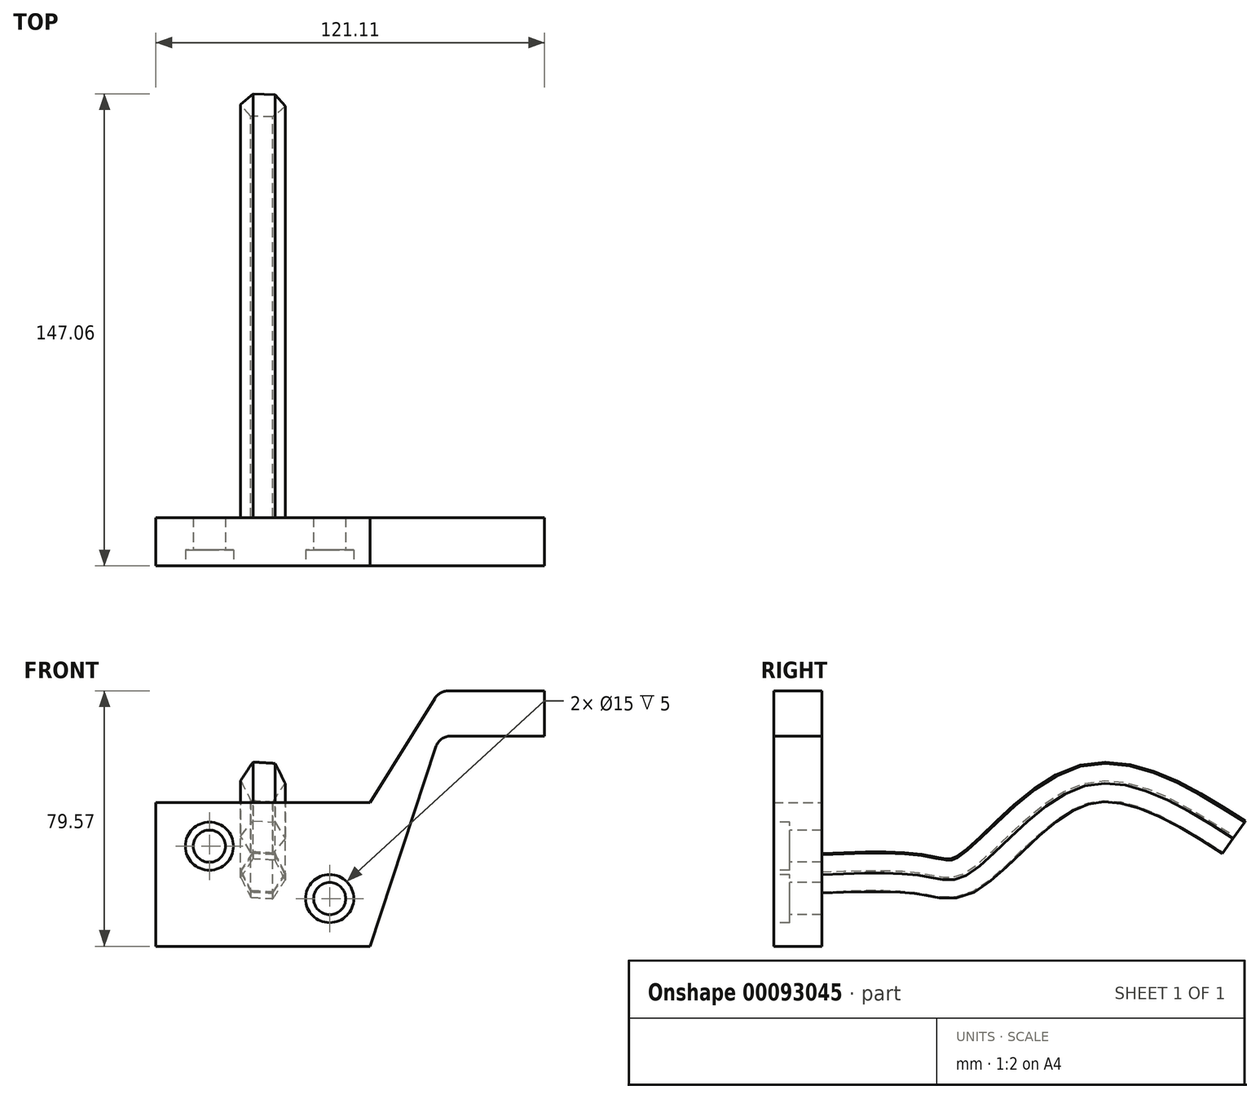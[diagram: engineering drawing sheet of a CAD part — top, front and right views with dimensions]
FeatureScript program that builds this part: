
annotation { "Feature Type Name" : "Feature", "Feature Type Description" : "" }
export const myFeature = defineFeature(function(context is Context, id is Id, definition is map)
    precondition{}
    {
        {
            var Q0;
            Q0=qCreatedBy(makeId("Front.planeOp"),FACE);
            var sketch = newSketch(context, id + "F0", { "sketchPlane" : qUnion([Q0])});
            skLineSegment(sketch, "E0.bottom", {"start": v(33.35, 22.38) * mm, "end": v(-33.35, 22.38) * mm});
            skLineSegment(sketch, "E0.top", {"start": v(33.35, -22.38) * mm, "end": v(-33.35, -22.38) * mm});
            skLineSegment(sketch, "E0.right", {"start": v(-33.35, 22.38) * mm, "end": v(-33.35, -22.38) * mm});
            skPoint(sketch, "E0.middle", {"position": v(0, 0) * mm});
            skLineSegment(sketch, "E1.bottom", {"start": v(87.76, 43.15) * mm, "end": v(55, 43.15) * mm});
            skLineSegment(sketch, "E1.top", {"start": v(87.76, 57.2) * mm, "end": v(55, 57.2) * mm});
            skLineSegment(sketch, "E1.left", {"start": v(87.76, 43.15) * mm, "end": v(87.76, 57.2) * mm});
            skPoint(sketch, "E1.middle", {"position": v(71.38, 50.17) * mm});
            skLineSegment(sketch, "E2", {"start": v(33.35, 22.38) * mm, "end": v(55, 57.2) * mm});
            skLineSegment(sketch, "E3", {"start": v(33.35, -22.38) * mm, "end": v(55, 43.15) * mm});
            skSolve(sketch);
        }
        {
            var Q0;
            Q0=makeQuery(id+"F0.imprint","IMPRINT",FACE,{"disambiguationData":[TD([[makeQuery(id+"F0.imprint","IMPRINT",EDGE,{"derivedFrom":sQuery(id+"F0.wireOp",EDGE,"E0.bottom")}),1.0]])]});
            extrude(context, id + "F1", {"entities" : qUnion([Q0]), "endBound" : BoundingType.SYMMETRIC, "depth" : 15 * mm});
        }
        {
            var Q0;
            Q0=makeQuery(id+"F1.opExtrude","CAP_FACE",FACE,{"disambiguationData":[OSD([sQuery(id+"F0.wireOp",EDGE,"E0.bottom"),sQuery(id+"F0.wireOp",EDGE,"E0.top"),sQuery(id+"F0.wireOp",EDGE,"E0.right"),sQuery(id+"F0.wireOp",EDGE,"E1.bottom"),sQuery(id+"F0.wireOp",EDGE,"E1.top"),sQuery(id+"F0.wireOp",EDGE,"E1.left"),sQuery(id+"F0.wireOp",EDGE,"E2"),sQuery(id+"F0.wireOp",EDGE,"E3")])],"isStart":false});
            var sketch = newSketch(context, id + "F2", { "sketchPlane" : qUnion([Q0])});
            skPoint(sketch, "E4", {"position": v(-16.69, 8.82) * mm});
            skPoint(sketch, "E5", {"position": v(20.81, -7.52) * mm});
            skSolve(sketch);
        }
        {
            var Q0;
            Q0=sQuery(id+"F2.wireOp",VERTEX,"E4");
            var Q1;
            Q1=sQuery(id+"F2.wireOp",VERTEX,"E5");
            var Q2;
            Q2=makeQuery(id+"F1.opExtrude","SWEPT_BODY",BODY,{"disambiguationData":[OSD([sQuery(id+"F0.wireOp",EDGE,"E0.bottom"),sQuery(id+"F0.wireOp",EDGE,"E0.top"),sQuery(id+"F0.wireOp",EDGE,"E0.right"),sQuery(id+"F0.wireOp",EDGE,"E1.bottom"),sQuery(id+"F0.wireOp",EDGE,"E1.top"),sQuery(id+"F0.wireOp",EDGE,"E1.left"),sQuery(id+"F0.wireOp",EDGE,"E2"),sQuery(id+"F0.wireOp",EDGE,"E3")])]});
            hole(context, id + "F3", {"style" : HoleStyle.C_BORE, "endStyle" : HoleEndStyle.THROUGH, "holeDiameter" : 10 * mm, "cBoreDiameter" : 15 * mm, "cBoreDepth" : 5 * mm, "locations" : qUnion([Q0, Q1]), "scope" : qUnion([Q2]), "isTappedThrough" : true});
        }
        {
            var Q0;
            Q0=qCreatedBy(makeId("Right.planeOp"),FACE);
            var sketch = newSketch(context, id + "F4", { "sketchPlane" : qUnion([Q0])});
            skFitSpline(sketch, "E6", {"points": [v(0, 0) * mm, v(38.53, 0) * mm, v(52.2, 0) * mm, v(88, 27.6) * mm, v(135.98, 11.59) * mm], "startDerivative": vector(168.63, 8.39) * mm, "endDerivative": vector(164.93, -104.72) * mm});
            skSolve(sketch);
        }
        {
            var Q0;
            Q0=qCreatedBy(makeId("Front.planeOp"),FACE);
            var sketch = newSketch(context, id + "F5", { "sketchPlane" : qUnion([Q0])});
            skCircle(sketch, "E7.cCircle", {"center": v(0, 0) * mm, "radius": 6 * mm, "construction": true});
            skLineSegment(sketch, "E7.0", {"start": v(-3.82, -5.79) * mm, "end": v(-6.92, 0.4) * mm});
            skLineSegment(sketch, "E7.1", {"start": v(-6.92, 0.4) * mm, "end": v(-3.1, 6.2) * mm});
            skLineSegment(sketch, "E7.2", {"start": v(-3.1, 6.2) * mm, "end": v(3.82, 5.79) * mm});
            skLineSegment(sketch, "E7.3", {"start": v(3.82, 5.79) * mm, "end": v(6.92, -0.4) * mm});
            skLineSegment(sketch, "E7.4", {"start": v(6.92, -0.4) * mm, "end": v(3.1, -6.2) * mm});
            skLineSegment(sketch, "E7.5", {"start": v(3.1, -6.2) * mm, "end": v(-3.82, -5.79) * mm});
            skPoint(sketch, "E7.0.midPoint", {"position": v(-5.37, -2.69) * mm});
            skSolve(sketch);
        }
        {
            var Q0;
            Q0 = qSketchRegion(id + "F5", true);
            var Q1;
            Q1=sQuery(id+"F4.wireOp",EDGE,"E6");
            sweep(context, id + "F6", {"operationType" : NewBodyOperationType.ADD, "profiles" : qUnion([Q0]), "path" : qUnion([Q1])});
        }
        {
            var Q0;
            Q0=makeQuery(id+"F1.opExtrude","SWEPT_EDGE",EDGE,{"disambiguationData":[OSD([sQuery(id+"F0.wireOp",EDGE,"E1.top"),sQuery(id+"F0.wireOp",EDGE,"E2")])]});
            var Q1;
            Q1=makeQuery(id+"F1.opExtrude","SWEPT_EDGE",EDGE,{"disambiguationData":[OSD([sQuery(id+"F0.wireOp",EDGE,"E1.bottom"),sQuery(id+"F0.wireOp",EDGE,"E3")])]});
            fillet(context, id + "F7", {"entities" : qUnion([Q0, Q1]), "radius" : 5 * mm, "tangentPropagation" : true, "allowEdgeOverflow" : false});
        }
    });
